# Revit family: 3010240_3010240C_MAST 4.0M Ø60 PL160 + Fund. 3530160C
name_source: partatom
category: Lighting Fixtures
units: mm (PartAtom-declared; Revit-internal decimal feet)

## family parameters
Always vertical = Yes
Cut with Voids When Loaded = No
Light Source = No
Maintain Annotation Orientation = No
OmniClass Number = 23.80.70.14.21
OmniClass Title = Street and Roadway Lighting
Part Type = Normal
Room Calculation Point = No
Round Connector Dimension = Use Diameter
Shared = No
Work Plane-Based = No

## types (1)
- Avtrappede master
    Area = 2,95 m²
    Art.nr = 3680240
    Art.nr CombiCoat = 3010240C
    Art.nr VZN = 3010240
    Bunndiameter = Ø108
    CE-godkjent = Ja
    Category = Avtrappede master
    Center of Gravity = X: -0,007 mm Y: 1,378 mm Z: 819,804 mm
    Default Elevation = 0 mm  [stored 0 ft]
    Density = 7449,65 kg/m³
    Description = MAST 4.0M Ø60 PL160 + Fund. 3530160C
    Design Status = 1
    Designer = khk
    EL nr CombiCoat = 3640047
    El nr VZN = 3640006
    Filnamn-VO = L10083
    Filnavn = MAST 4.0M Ø60 PL160 + Fund. 3530160C
    Fotplate C/C bolter = 160mm
    Fundament = 3530160C
    Lyspunkthoyde = 4m
    Manufacturer = Vik Ørsta AS
    Mass = 35,93 kg
    Materialkvalitet = S355
    Model = 3010240_3010240C
    Part Number = L10257
    Requested Accuracy = Low
    Revision Number = -
    Size = 210mmX210mmX6021,6mm
    Sti&Filnamn-VO = L10083
    Title = MAST 4.0M Ø60 PL160 + Fund. 3530160C
    Toppdiameter = Ø60
    Volume = 0,00 m³

note: [stored X ft] marks values corroborated as IEEE doubles in the binary element streams (Revit-internal decimal feet)

## geometry (parser evidence)
native form markers: Sweep x3
no freeform markers — native parametric forms only
